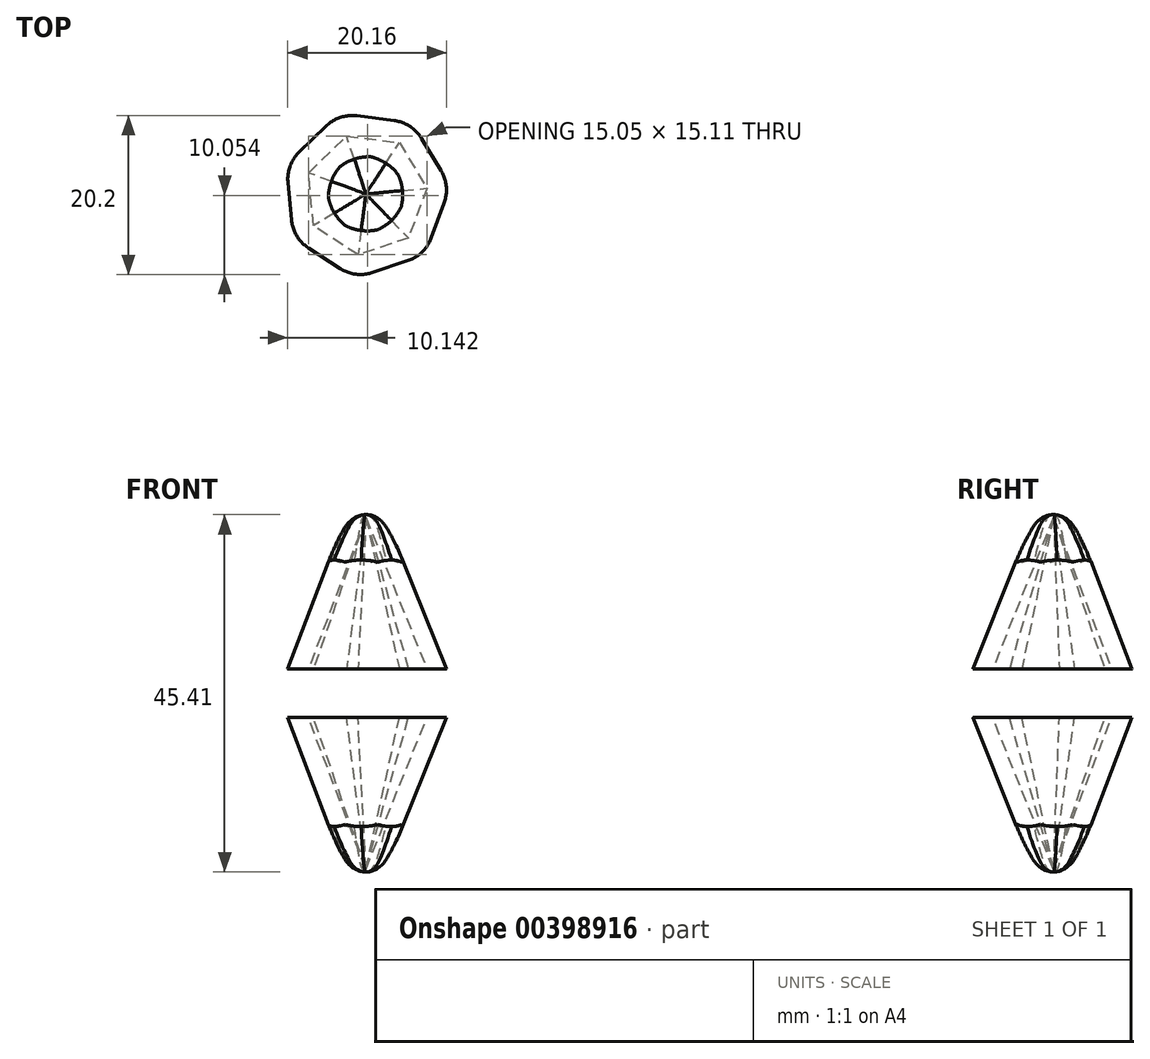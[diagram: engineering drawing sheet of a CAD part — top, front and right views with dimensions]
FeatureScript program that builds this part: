
annotation { "Feature Type Name" : "Feature", "Feature Type Description" : "" }
export const myFeature = defineFeature(function(context is Context, id is Id, definition is map)
    precondition{}
    {
        {
            var Q0;
            Q0=qCreatedBy(makeId("Top.planeOp"),FACE);
            var sketch = newSketch(context, id + "F0", { "sketchPlane" : qUnion([Q0])});
            skCircle(sketch, "E0.cCircle", {"center": v(0, 0) * mm, "radius": 9.72 * mm, "construction": true});
            skLineSegment(sketch, "E0.0", {"start": v(-10.12, 3.73) * mm, "end": v(-3.4, 10.24) * mm});
            skLineSegment(sketch, "E0.1", {"start": v(-3.4, 10.24) * mm, "end": v(5.89, 9.04) * mm});
            skLineSegment(sketch, "E0.2", {"start": v(5.89, 9.04) * mm, "end": v(10.73, 1.03) * mm});
            skLineSegment(sketch, "E0.3", {"start": v(10.73, 1.03) * mm, "end": v(7.5, -7.75) * mm});
            skLineSegment(sketch, "E0.4", {"start": v(7.5, -7.75) * mm, "end": v(-1.38, -10.7) * mm});
            skLineSegment(sketch, "E0.5", {"start": v(-1.38, -10.7) * mm, "end": v(-9.22, -5.59) * mm});
            skLineSegment(sketch, "E0.6", {"start": v(-9.22, -5.59) * mm, "end": v(-10.12, 3.73) * mm});
            skPoint(sketch, "E0.0.midPoint", {"position": v(-6.76, 6.98) * mm});
            skSolve(sketch);
        }
        {
            var Q0;
            Q0=makeQuery(id+"F0.imprint","IMPRINT",FACE,{"disambiguationData":[TD([[makeQuery(id+"F0.imprint","IMPRINT",EDGE,{"derivedFrom":sQuery(id+"F0.wireOp",EDGE,"E0.0")}),-1.0]])]});
            extrude(context, id + "F1", {"entities" : qUnion([Q0]), "depth" : 30.48 * mm, "hasDraft" : true, "draftAngle" : 20 * degree, "draftPullDirection" : true});
        }
        {
            var Q0;
            Q0=makeQuery(id+"F1.opExtrude","CAP_FACE",FACE,{"disambiguationData":[OSD([sQuery(id+"F0.wireOp",EDGE,"E0.0"),sQuery(id+"F0.wireOp",EDGE,"E0.1"),sQuery(id+"F0.wireOp",EDGE,"E0.2"),sQuery(id+"F0.wireOp",EDGE,"E0.3"),sQuery(id+"F0.wireOp",EDGE,"E0.4"),sQuery(id+"F0.wireOp",EDGE,"E0.5"),sQuery(id+"F0.wireOp",EDGE,"E0.6")])],"isStart":true});
            shell(context, id + "F2", {"entities" : qUnion([Q0]), "thickness" : 2.54 * mm});
        }
        {
            var Q0;
            Q0=makeQuery(id+"F1.opExtrude","SWEPT_EDGE",EDGE,{"disambiguationData":[OSD([sQuery(id+"F0.wireOp",EDGE,"E0.0"),sQuery(id+"F0.wireOp",EDGE,"E0.1")])]});
            var Q1;
            Q1=makeQuery(id+"F1.opExtrude","SWEPT_EDGE",EDGE,{"disambiguationData":[OSD([sQuery(id+"F0.wireOp",EDGE,"E0.1"),sQuery(id+"F0.wireOp",EDGE,"E0.2")])]});
            var Q2;
            Q2=makeQuery(id+"F1.opExtrude","SWEPT_EDGE",EDGE,{"disambiguationData":[OSD([sQuery(id+"F0.wireOp",EDGE,"E0.0"),sQuery(id+"F0.wireOp",EDGE,"E0.6")])]});
            var Q3;
            Q3=makeQuery(id+"F1.opExtrude","SWEPT_EDGE",EDGE,{"disambiguationData":[OSD([sQuery(id+"F0.wireOp",EDGE,"E0.5"),sQuery(id+"F0.wireOp",EDGE,"E0.6")])]});
            var Q4;
            Q4=makeQuery(id+"F1.opExtrude","SWEPT_EDGE",EDGE,{"disambiguationData":[OSD([sQuery(id+"F0.wireOp",EDGE,"E0.2"),sQuery(id+"F0.wireOp",EDGE,"E0.3")])]});
            var Q5;
            Q5=makeQuery(id+"F1.opExtrude","SWEPT_EDGE",EDGE,{"disambiguationData":[OSD([sQuery(id+"F0.wireOp",EDGE,"E0.3"),sQuery(id+"F0.wireOp",EDGE,"E0.4")])]});
            var Q6;
            Q6=makeQuery(id+"F1.opExtrude","SWEPT_EDGE",EDGE,{"disambiguationData":[OSD([sQuery(id+"F0.wireOp",EDGE,"E0.4"),sQuery(id+"F0.wireOp",EDGE,"E0.5")])]});
            fillet(context, id + "F3", {"entities" : qUnion([Q0, Q1, Q2, Q3, Q4, Q5, Q6]), "radius" : 5.08 * mm, "tangentPropagation" : true, "allowEdgeOverflow" : false});
        }
        {
            var Q0;
            Q0=makeQuery(id+"F1.opExtrude","SWEPT_BODY",BODY,{"disambiguationData":[OSD([sQuery(id+"F0.wireOp",EDGE,"E0.0"),sQuery(id+"F0.wireOp",EDGE,"E0.1"),sQuery(id+"F0.wireOp",EDGE,"E0.2"),sQuery(id+"F0.wireOp",EDGE,"E0.3"),sQuery(id+"F0.wireOp",EDGE,"E0.4"),sQuery(id+"F0.wireOp",EDGE,"E0.5"),sQuery(id+"F0.wireOp",EDGE,"E0.6")])]});
            var Q1;
            Q1=makeQuery(id+"F1.opExtrude","CAP_FACE",FACE,{"disambiguationData":[OSD([sQuery(id+"F0.wireOp",EDGE,"E0.0"),sQuery(id+"F0.wireOp",EDGE,"E0.1"),sQuery(id+"F0.wireOp",EDGE,"E0.2"),sQuery(id+"F0.wireOp",EDGE,"E0.3"),sQuery(id+"F0.wireOp",EDGE,"E0.4"),sQuery(id+"F0.wireOp",EDGE,"E0.5"),sQuery(id+"F0.wireOp",EDGE,"E0.6")])],"isStart":true});
            mirror(context, id + "F4", {"entities" : qUnion([Q0]), "mirrorPlane" : qUnion([Q1])});
        }
        {
            var Q0;
            Q0=makeQuery(id+"F1.opExtrude","SWEPT_BODY",BODY,{"disambiguationData":[OSD([sQuery(id+"F0.wireOp",EDGE,"E0.0"),sQuery(id+"F0.wireOp",EDGE,"E0.1"),sQuery(id+"F0.wireOp",EDGE,"E0.2"),sQuery(id+"F0.wireOp",EDGE,"E0.3"),sQuery(id+"F0.wireOp",EDGE,"E0.4"),sQuery(id+"F0.wireOp",EDGE,"E0.5"),sQuery(id+"F0.wireOp",EDGE,"E0.6")])]});
            transform(context, id + "F5", {"entities" : qUnion([Q0]), "transformType" : TransformType.TRANSLATION_3D, "dx" : 0 * mm, "dy" : 0 * mm, "dz" : 6.17 * mm, "makeCopy" : false});
        }
    });
